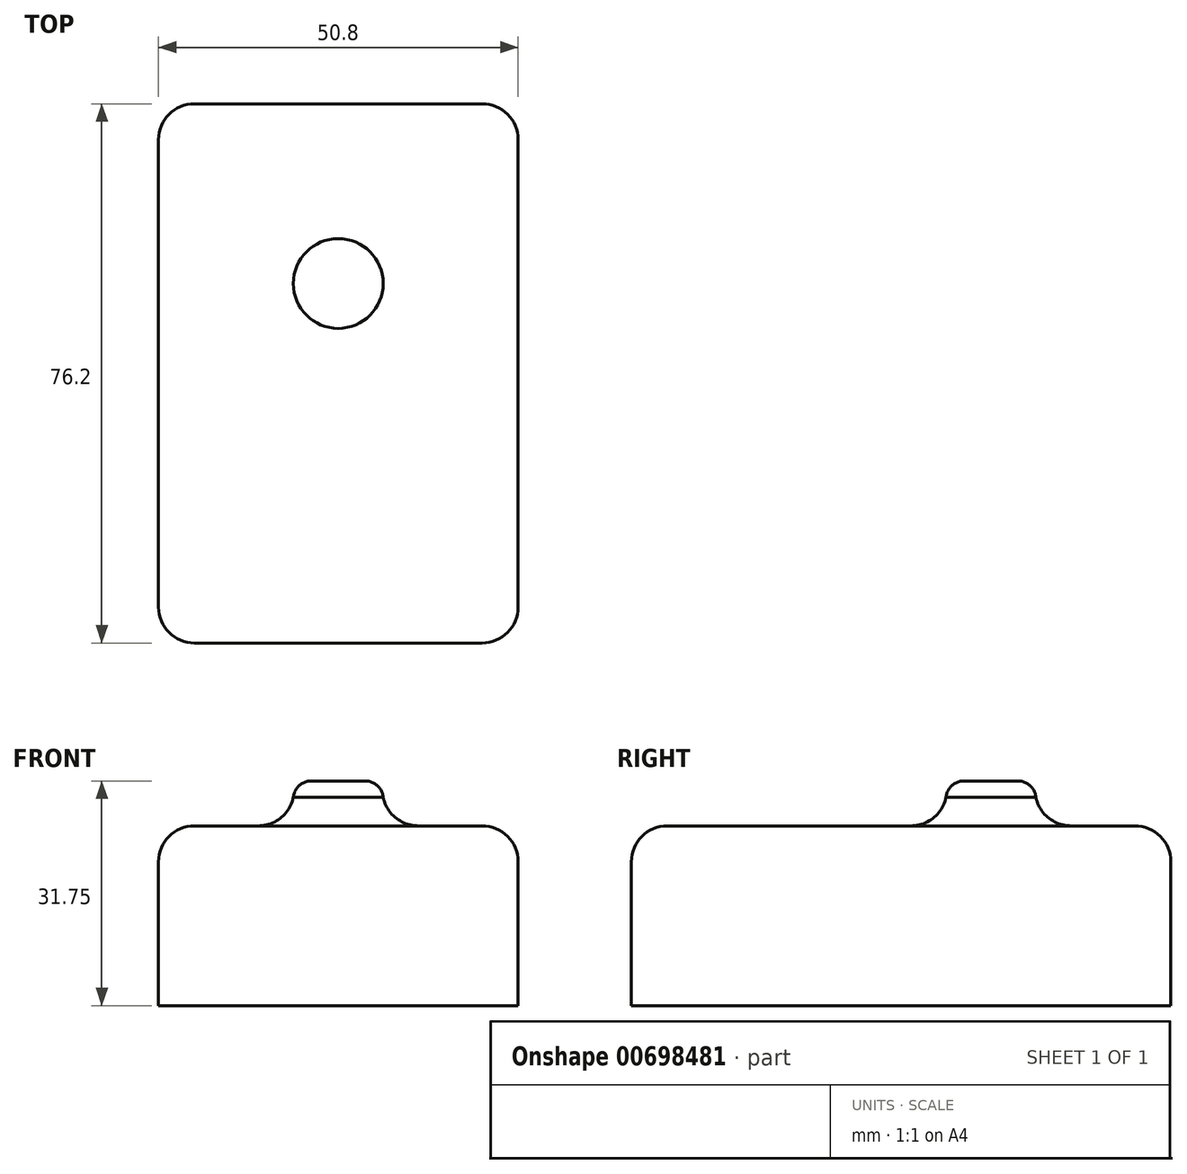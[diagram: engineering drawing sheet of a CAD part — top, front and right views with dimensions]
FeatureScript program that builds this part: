
annotation { "Feature Type Name" : "Feature", "Feature Type Description" : "" }
export const myFeature = defineFeature(function(context is Context, id is Id, definition is map)
    precondition{}
    {
        {
            var Q0;
            Q0=qCreatedBy(makeId("Front.planeOp"),FACE);
            var sketch = newSketch(context, id + "F0", { "sketchPlane" : qUnion([Q0])});
            skLineSegment(sketch, "E0.bottom", {"start": v(50.8, 25.4) * mm, "end": v(0, 25.4) * mm});
            skLineSegment(sketch, "E0.top", {"start": v(50.8, 0) * mm, "end": v(0, 0) * mm});
            skLineSegment(sketch, "E0.left", {"start": v(50.8, 25.4) * mm, "end": v(50.8, 0) * mm});
            skLineSegment(sketch, "E0.right", {"start": v(0, 25.4) * mm, "end": v(0, 0) * mm});
            skSolve(sketch);
        }
        {
            var Q0;
            Q0=makeQuery(id+"F0.imprint","IMPRINT",FACE,{"disambiguationData":[TD([[makeQuery(id+"F0.imprint","IMPRINT",EDGE,{"derivedFrom":sQuery(id+"F0.wireOp",EDGE,"E0.bottom")}),1.0]])]});
            extrude(context, id + "F1", {"entities" : qUnion([Q0]), "depth" : 76.2 * mm, "offsetDistance" : 25.4 * mm});
        }
        {
            var Q0;
            Q0=makeQuery(id+"F1.opExtrude","SWEPT_FACE",FACE,{"disambiguationData":[OSD([sQuery(id+"F0.wireOp",EDGE,"E0.bottom")])]});
            var sketch = newSketch(context, id + "F2", { "sketchPlane" : qUnion([Q0])});
            skCircle(sketch, "E1", {"center": v(25.4, -25.4) * mm, "radius": 6.35 * mm});
            skSolve(sketch);
        }
        {
            var Q0;
            Q0 = qSketchRegion(id + "F2", true);
            extrude(context, id + "F3", {"entities" : qUnion([Q0]), "operationType" : NewBodyOperationType.ADD, "depth" : 6.35 * mm, "offsetDistance" : 25.4 * mm});
        }
        {
            var Q0;
            Q0=makeQuery(id+"F3.opExtrude","CAP_EDGE",EDGE,{"disambiguationData":[OSD([sQuery(id+"F2.wireOp",EDGE,"E1")])],"isStart":true});
            var Q1;
            Q1=makeQuery(id+"F3.opExtrude","CAP_EDGE",EDGE,{"disambiguationData":[OSD([sQuery(id+"F2.wireOp",EDGE,"E1")])],"isStart":false});
            fillet(context, id + "F4", {"entities" : qUnion([Q0, Q1]), "radius" : 2.54 * mm, "tangentPropagation" : true, "allowEdgeOverflow" : false});
        }
        {
            var Q0;
            Q0=makeQuery(id+"F1.opExtrude","CAP_EDGE",EDGE,{"disambiguationData":[OSD([sQuery(id+"F0.wireOp",EDGE,"E0.left")])],"isStart":false});
            var Q1;
            Q1=makeQuery(id+"F1.opExtrude","CAP_EDGE",EDGE,{"disambiguationData":[OSD([sQuery(id+"F0.wireOp",EDGE,"E0.left")])],"isStart":true});
            var Q2;
            Q2=makeQuery(id+"F1.opExtrude","CAP_EDGE",EDGE,{"disambiguationData":[OSD([sQuery(id+"F0.wireOp",EDGE,"E0.right")])],"isStart":true});
            var Q3;
            Q3=makeQuery(id+"F1.opExtrude","CAP_EDGE",EDGE,{"disambiguationData":[OSD([sQuery(id+"F0.wireOp",EDGE,"E0.right")])],"isStart":false});
            var Q4;
            Q4=makeQuery(id+"F1.opExtrude","SWEPT_FACE",FACE,{"disambiguationData":[OSD([sQuery(id+"F0.wireOp",EDGE,"E0.bottom")])]});
            fillet(context, id + "F5", {"entities" : qUnion([Q0, Q1, Q2, Q3, Q4]), "radius" : 5.08 * mm, "tangentPropagation" : true, "allowEdgeOverflow" : false});
        }
    });
